# Revit family: FU_Config_Sandler_Kern 3080
name_source: partatom
category: Furniture
units: mm (PartAtom-declared; Revit-internal decimal feet)

## family parameters
Always vertical = Yes
Cut with Voids When Loaded = No
OmniClass Number = 23.40.20.00
OmniClass Title = General Furniture and Specialties
Render Appearance Source = Family Geometry
Room Calculation Point = No
Shared = No
Work Plane-Based = No

## types (1)
- Kern 3080
    Default Elevation = 0 mm  [stored 0 ft]
    Depth = 1420 mm  [stored 4.65879 ft]
    Description = Room Configuration 8: four-seat room with privacy screens on three sides. Consists of 2 two-seat corner units (KER0222 and KER0224), 2 rear privacy screens (KER1222PC and KER1224PC), and 1 narrow connecting panel (KER2070). 87.4"/222cm wide, 55.9"/142cm deep.
    Height = 1260 mm  [stored 4.13386 ft]
    Manufacturer = Sandler
    Model = Kern 3080
    Panel = Fabric - Mainline Flax - Kensington MLF07
    URL = https://www.sandlerseating.com
    Width = 2070 mm  [stored 6.79134 ft]

note: [stored X ft] marks values corroborated as IEEE doubles in the binary element streams (Revit-internal decimal feet)

## geometry (parser evidence)
native form markers: Sweep x25
no freeform markers — native parametric forms only
